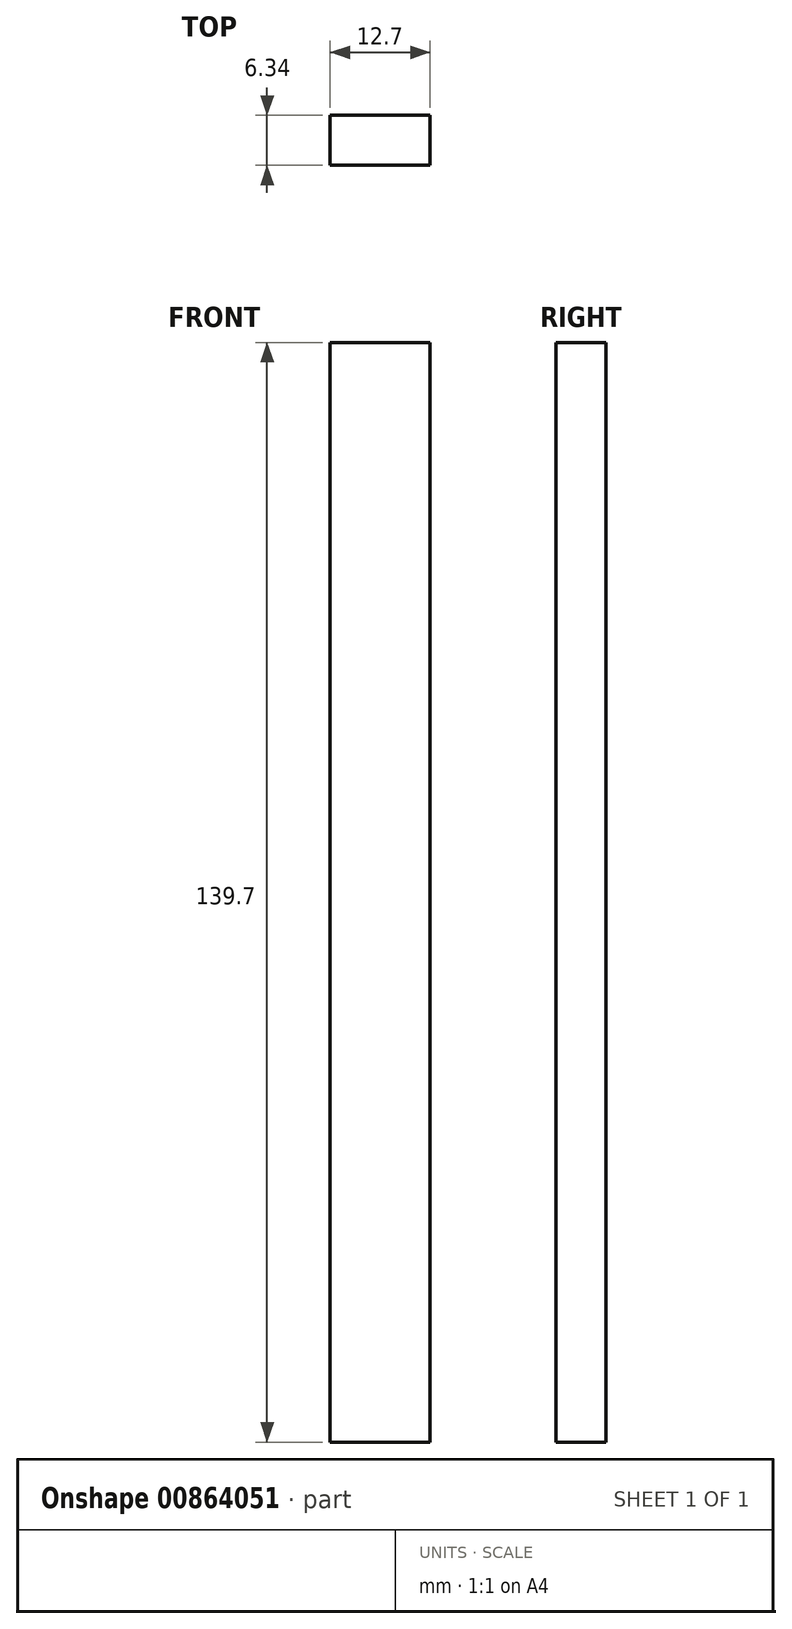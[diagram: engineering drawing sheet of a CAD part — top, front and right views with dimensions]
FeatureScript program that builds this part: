
annotation { "Feature Type Name" : "Feature", "Feature Type Description" : "" }
export const myFeature = defineFeature(function(context is Context, id is Id, definition is map)
    precondition{}
    {
        {
            var Q0;
            Q0=qCreatedBy(makeId("Top.planeOp"),FACE);
            var sketch = newSketch(context, id + "F0", { "sketchPlane" : qUnion([Q0])});
            skLineSegment(sketch, "E0.bottom", {"start": v(6.35, 3.17) * mm, "end": v(-6.35, 3.17) * mm});
            skLineSegment(sketch, "E0.top", {"start": v(6.35, -3.18) * mm, "end": v(-6.35, -3.18) * mm});
            skLineSegment(sketch, "E0.left", {"start": v(6.35, 3.18) * mm, "end": v(6.35, -3.18) * mm});
            skLineSegment(sketch, "E0.right", {"start": v(-6.35, 3.17) * mm, "end": v(-6.35, -3.18) * mm});
            skPoint(sketch, "E0.middle", {"position": v(0, 0) * mm});
            skSolve(sketch);
        }
        {
            var Q0;
            Q0=makeQuery(id+"F0.imprint","IMPRINT",FACE,{"disambiguationData":[TD([[makeQuery(id+"F0.imprint","IMPRINT",EDGE,{"derivedFrom":sQuery(id+"F0.wireOp",EDGE,"E0.bottom")}),1.0]])]});
            extrude(context, id + "F1", {"entities" : qUnion([Q0]), "depth" : 139.7 * mm, "offsetDistance" : 25.4 * mm});
        }
    });
